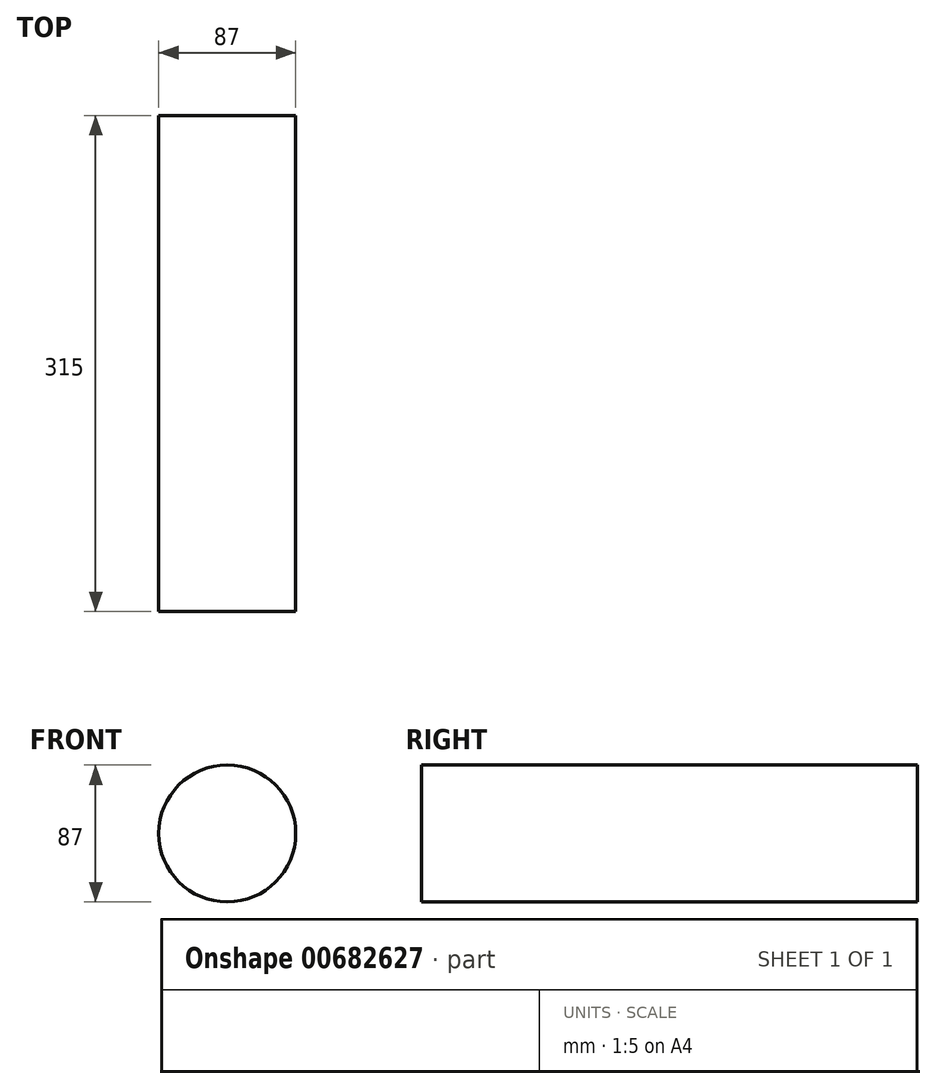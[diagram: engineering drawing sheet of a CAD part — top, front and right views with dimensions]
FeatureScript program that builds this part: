
annotation { "Feature Type Name" : "Feature", "Feature Type Description" : "" }
export const myFeature = defineFeature(function(context is Context, id is Id, definition is map)
    precondition{}
    {
        {
            var Q0;
            Q0=qCreatedBy(makeId("Front.planeOp"),FACE);
            var sketch = newSketch(context, id + "F0", { "sketchPlane" : qUnion([Q0])});
            skCircle(sketch, "E0", {"center": v(0, 0) * mm, "radius": 43.5 * mm});
            skSolve(sketch);
        }
        {
            var Q0;
            Q0=makeQuery(id+"F0.imprint","IMPRINT",FACE,{"disambiguationData":[TD([[makeQuery(id+"F0.imprint","IMPRINT",EDGE,{"derivedFrom":sQuery(id+"F0.wireOp",EDGE,"E0")}),1.0]])]});
            extrude(context, id + "F1", {"entities" : qUnion([Q0]), "depth" : 315 * mm, "offsetDistance" : 25 * mm});
        }
    });
